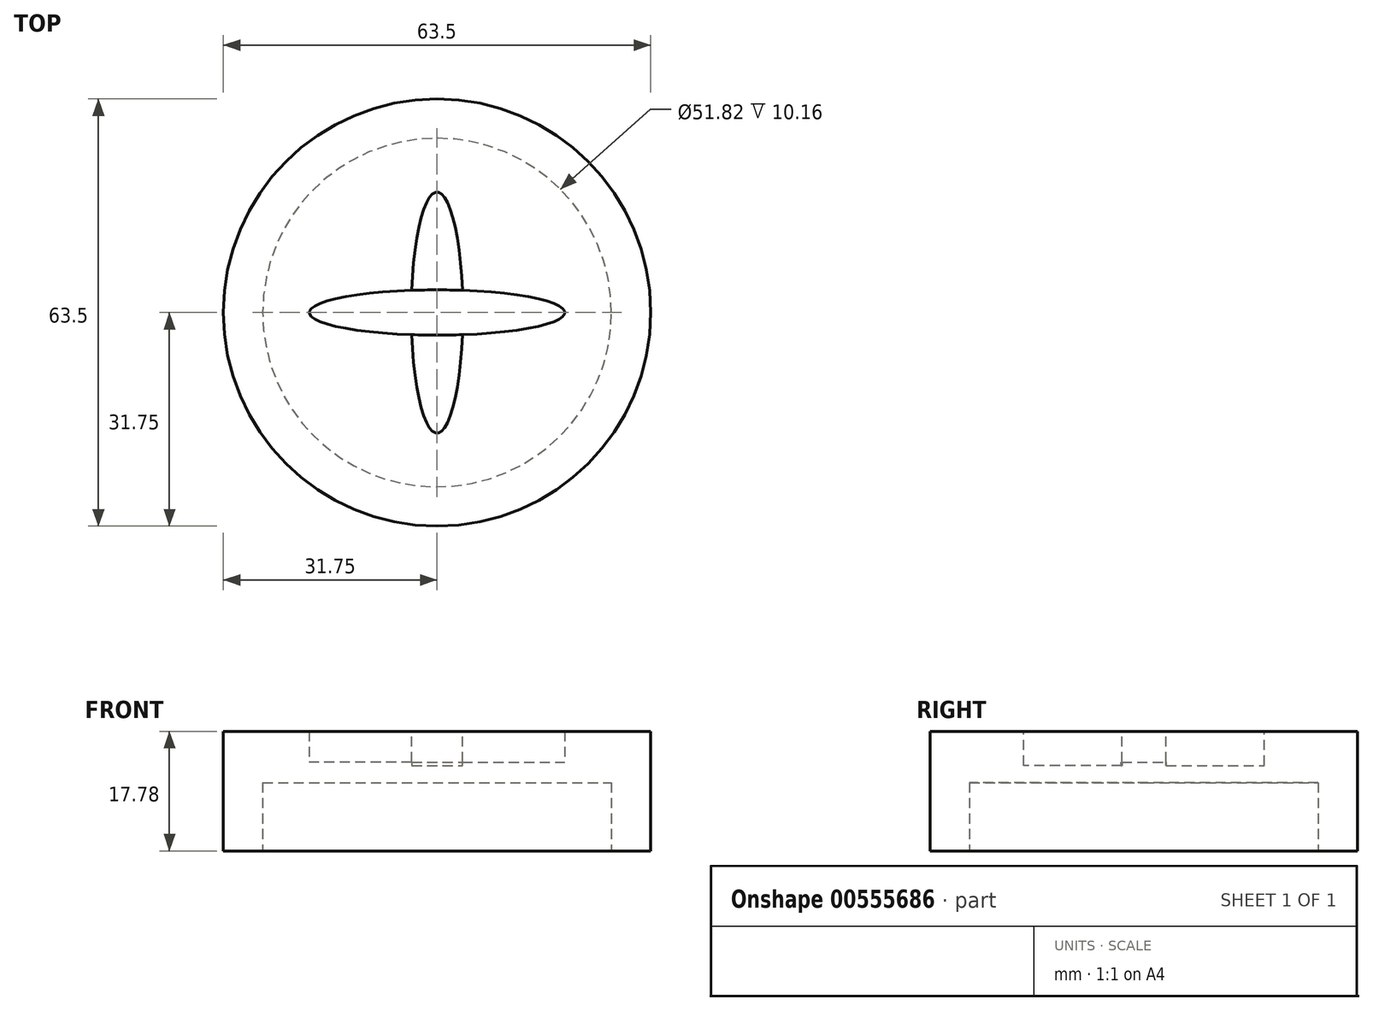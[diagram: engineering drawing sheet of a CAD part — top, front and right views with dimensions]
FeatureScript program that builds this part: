
annotation { "Feature Type Name" : "Feature", "Feature Type Description" : "" }
export const myFeature = defineFeature(function(context is Context, id is Id, definition is map)
    precondition{}
    {
        {
            var Q0;
            Q0=qCreatedBy(makeId("Top.planeOp"),FACE);
            var sketch = newSketch(context, id + "F0", { "sketchPlane" : qUnion([Q0])});
            skCircle(sketch, "E0", {"center": v(0, 0) * mm, "radius": 31.75 * mm});
            skSolve(sketch);
        }
        {
            var Q0;
            Q0=makeQuery(id+"F0.imprint","IMPRINT",FACE,{"disambiguationData":[TD([[makeQuery(id+"F0.imprint","IMPRINT",EDGE,{"derivedFrom":sQuery(id+"F0.wireOp",EDGE,"E0")}),1.0]])]});
            extrude(context, id + "F1", {"entities" : qUnion([Q0]), "depth" : 17.78 * mm});
        }
        {
            var Q0;
            Q0=makeQuery(id+"F1.opExtrude","CAP_FACE",FACE,{"disambiguationData":[OSD([sQuery(id+"F0.wireOp",EDGE,"E0")])],"isStart":true});
            var sketch = newSketch(context, id + "F2", { "sketchPlane" : qUnion([Q0])});
            skCircle(sketch, "E1", {"center": v(0, 0) * mm, "radius": 25.9 * mm});
            skSolve(sketch);
        }
        {
            var Q0;
            Q0=qSketchRegion(id+"F2",true);
            extrude(context, id + "F3", {"entities" : qUnion([Q0]), "operationType" : NewBodyOperationType.REMOVE, "oppositeDirection" : true, "depth" : 10.16 * mm});
        }
        {
            var Q0;
            Q0=makeQuery(id+"F1.opExtrude","CAP_FACE",FACE,{"disambiguationData":[OSD([sQuery(id+"F0.wireOp",EDGE,"E0")])],"isStart":false});
            var sketch = newSketch(context, id + "F4", { "sketchPlane" : qUnion([Q0])});
            skEllipse(sketch, "E2", {"center": v(0, 0) * mm, "majorRadius": 18.98 * mm, "minorRadius": 3.36 * mm, "majorAxis": v(-1, 0)});
            skSolve(sketch);
        }
        {
            var Q0;
            Q0=makeQuery(id+"F4.imprint","IMPRINT",FACE,{"disambiguationData":[TD([[makeQuery(id+"F4.imprint","IMPRINT",EDGE,{"derivedFrom":sQuery(id+"F4.wireOp",EDGE,"E2")}),1.0]])]});
            var Q1;
            Q1=sQuery(id+"F4.wireOp",EDGE,"E2");
            extrude(context, id + "F5", {"entities" : qUnion([Q0]), "operationType" : NewBodyOperationType.REMOVE, "surfaceEntities" : qUnion([Q1]), "oppositeDirection" : true, "depth" : 4.57 * mm, "offsetDistance" : 25.4 * mm});
        }
        {
            var Q0;
            Q0=makeQuery(id+"F1.opExtrude","CAP_FACE",FACE,{"disambiguationData":[OSD([sQuery(id+"F0.wireOp",EDGE,"E0")])],"isStart":false});
            var sketch = newSketch(context, id + "F6", { "sketchPlane" : qUnion([Q0])});
            skEllipse(sketch, "E3", {"center": v(0, 0) * mm, "majorRadius": 17.9 * mm, "minorRadius": 3.83 * mm, "majorAxis": v(0, 1)});
            skSolve(sketch);
        }
        {
            var Q0;
            {var subQ0=sQuery(id+"F6.wireOp",EDGE,"E3");var subQ1=makeQuery(id+"F5.boolean.opBoolean","COPY",EDGE,{"derivedFrom":makeQuery(id+"F5.opExtrude","CAP_EDGE",EDGE,{"disambiguationData":[OSD([sQuery(id+"F4.wireOp",EDGE,"E2")])],"isStart":true})});var subQ2=makeQuery(id+"F6.imprint","INTERSECT",VERTEX,{"disambiguationData":[OD(1.0)],"derivedFrom":[subQ1,subQ0]});Q0=makeQuery(id+"F6.imprint","IMPRINT",FACE,{"disambiguationData":[TD([[makeQuery(id+"F6.imprint","IMPRINT",EDGE,{"disambiguationData":[TD([[subQ2,1.0]])],"derivedFrom":subQ0}),1.0]])]});}
            var Q1;
            {var subQ0=sQuery(id+"F6.wireOp",EDGE,"E3");var subQ1=makeQuery(id+"F5.boolean.opBoolean","COPY",EDGE,{"derivedFrom":makeQuery(id+"F5.opExtrude","CAP_EDGE",EDGE,{"disambiguationData":[OSD([sQuery(id+"F4.wireOp",EDGE,"E2")])],"isStart":true})});var subQ2=makeQuery(id+"F6.imprint","INTERSECT",VERTEX,{"disambiguationData":[OD(0.0)],"derivedFrom":[subQ1,subQ0]});Q1=makeQuery(id+"F6.imprint","IMPRINT",FACE,{"disambiguationData":[TD([[makeQuery(id+"F6.imprint","IMPRINT",EDGE,{"disambiguationData":[TD([[subQ2,-1.0]])],"derivedFrom":subQ0}),1.0]])]});}
            var Q2;
            Q2=sQuery(id+"F6.wireOp",EDGE,"E3");
            extrude(context, id + "F7", {"entities" : qUnion([Q0, Q1]), "operationType" : NewBodyOperationType.REMOVE, "surfaceEntities" : qUnion([Q2]), "oppositeDirection" : true, "depth" : 5.08 * mm, "offsetDistance" : 25.4 * mm});
        }
    });
